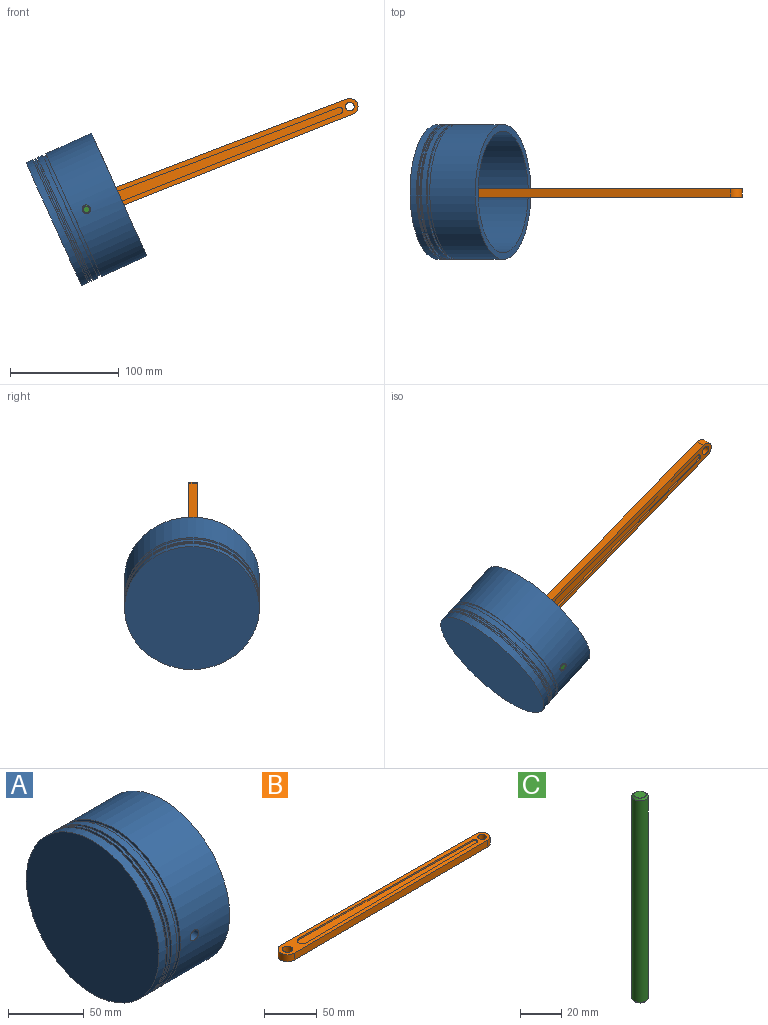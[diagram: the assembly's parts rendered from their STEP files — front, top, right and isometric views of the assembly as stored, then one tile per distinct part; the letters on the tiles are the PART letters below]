
ASSEMBLY  parts=3 mates=3
PART A: 19 faces, bbox 66x124x124 mm
  f0: cylinder r=56mm len=112mm, axis (-1,0,0), area 21010.4mm2, adj f11,f12,f13,f14
  f1: plane 124x124mm, normal (-1,0,0), area 12076.3mm2, adj f2
  f2: cylinder r=62mm len=124mm, axis (-1,0,0), area 2597.1mm2, adj f1,f3
  f3: plane 124x124mm, normal (1,0,0), area 640.5mm2, adj f2,f15
  f4: plane 124x124mm, normal (-1,0,0), area 640.5mm2, adj f15,f16
  f5: plane 124x124mm, normal (1,0,0), area 640.5mm2, adj f16,f17
  f6: plane 124x124mm, normal (-1,0,0), area 640.5mm2, adj f17,f18
  f7: plane 124x124mm, normal (1,0,0), area 640.5mm2, adj f10,f18
  f8: plane 124x124mm, normal (-1,0,0), area 640.5mm2, adj f9,f10
  f9: cylinder r=62mm len=124mm, axis (-1,0,0), area 17818.1mm2, adj f8,f11,f13,f14
  f10: cylinder r=60.33mm len=120.67mm, axis (-1,0,0), area 1263.6mm2, adj f7,f8
  f11: cylinder r=4mm len=8mm, axis (0,1,0), area 150.8mm2, adj f0,f9
  f12: plane 112x112mm, normal (1,0,0), area 9852mm2, adj f0
  f13: plane 124x124mm, normal (1,0,0), area 2224.2mm2, adj f0,f9
  f14: cylinder r=4mm len=8mm, axis (0,1,0), area 150.8mm2, adj f0,f9
  f15: cylinder r=60.33mm len=120.67mm, axis (-1,0,0), area 631.8mm2, adj f3,f4
  f16: cylinder r=62mm len=124mm, axis (-1,0,0), area 649.3mm2, adj f4,f5
  f17: cylinder r=60.33mm len=120.67mm, axis (-1,0,0), area 631.8mm2, adj f5,f6
  f18: cylinder r=62mm len=124mm, axis (-1,0,0), area 1947.8mm2, adj f6,f7
PART B: 18 faces, bbox 276.5x18x8 mm
  f0: plane 238x10mm, normal (0,0,1), area 1893.5mm2, adj f2,f3,f4,f5
  f1: plane 238x10mm, normal (0,0,-1), area 1893.5mm2, adj f7,f8,f9,f10
  f2: plane 229.98x2mm, normal (-0.01,1,0), area 383.3mm2, adj f0,f3,f5,f15
  f3: cylinder r=5mm len=10mm, axis (0,0,-1), area 26.3mm2, adj f0,f2,f4,f15
  f4: plane 229.98x2mm, normal (-0.01,-1,0), area 383.3mm2, adj f0,f3,f5,f15
  f5: cylinder r=3mm len=6mm, axis (0,0,-1), area 15.6mm2, adj f0,f2,f4,f15
  f6: cylinder r=4mm len=8mm, axis (0,0,1), area 201.1mm2, adj f15,f16
  f7: plane 229.98x2mm, normal (-0.01,1,0), area 383.3mm2, adj f1,f8,f10,f16
  f8: cylinder r=5mm len=10mm, axis (0,0,-1), area 26.3mm2, adj f1,f7,f9,f16
  f9: plane 229.98x2mm, normal (-0.01,-1,0), area 383.3mm2, adj f1,f8,f10,f16
  f10: cylinder r=3mm len=6mm, axis (0,0,-1), area 15.6mm2, adj f1,f7,f9,f16
  f11: cylinder r=9mm len=18mm, axis (0,0,1), area 227mm2, adj f12,f14,f15,f16
  f12: plane 259.99x8mm, normal (0.01,-1,0), area 2080mm2, adj f11,f13,f15,f16
  f13: cylinder r=7.5mm len=15mm, axis (0,0,1), area 187.8mm2, adj f12,f14,f15,f16
  f14: plane 259.99x8mm, normal (0.01,1,0), area 2080mm2, adj f11,f13,f15,f16
  f15: plane 276.5x18mm, normal (0,0,1), area 2483.4mm2, adj f2,f3,f4,f5,f6,f11,f12,f13
  f16: plane 276.5x18mm, normal (0,0,-1), area 2483.4mm2, adj f6,f7,f8,f9,f10,f11,f12,f13
  f17: cylinder r=5mm len=10mm, axis (0,0,1), area 251.3mm2, adj f15,f16
PART C: 5 faces, bbox 8x8x122 mm
  f0: plane 6x6mm, normal (0,0,-1), area 28.3mm2, adj f1
  f1: cone r=4mm half-angle=45deg, axis (0,0,1), area 31.1mm2, adj f0,f3
  f2: cone r=4mm half-angle=45deg, axis (0,0,-1), area 31.1mm2, adj f3,f4
  f3: cylinder r=4mm len=120mm, axis (0,0,-1), area 3015.9mm2, adj f1,f2
  f4: plane 6x6mm, normal (0,0,1), area 28.3mm2, adj f2
PLACE A rot(axis=(0,-1,0),24.3deg) t=(42.59,96.81,-42.26)mm
PLACE B rot(axis=(-0.97,-0.18,-0.18),92deg) t=(23.41,145.74,6.77)mm
PLACE C rot(axis=(-0.96,-0.21,-0.21),92.5deg) t=(22,145.74,3.31)mm
MATE fastened A.f11 <-> C.f3  axis (0,1,0) through (88.16,205.74,-21.67)mm
MATE cylindrical C.f3 <-> B.f11  axis (0,-1,0) through (88.16,145.74,-21.67)mm
MATE planar C.f3 <-> B.f11  axis (0,-1,0) through (88.16,145.74,-21.67)mm
